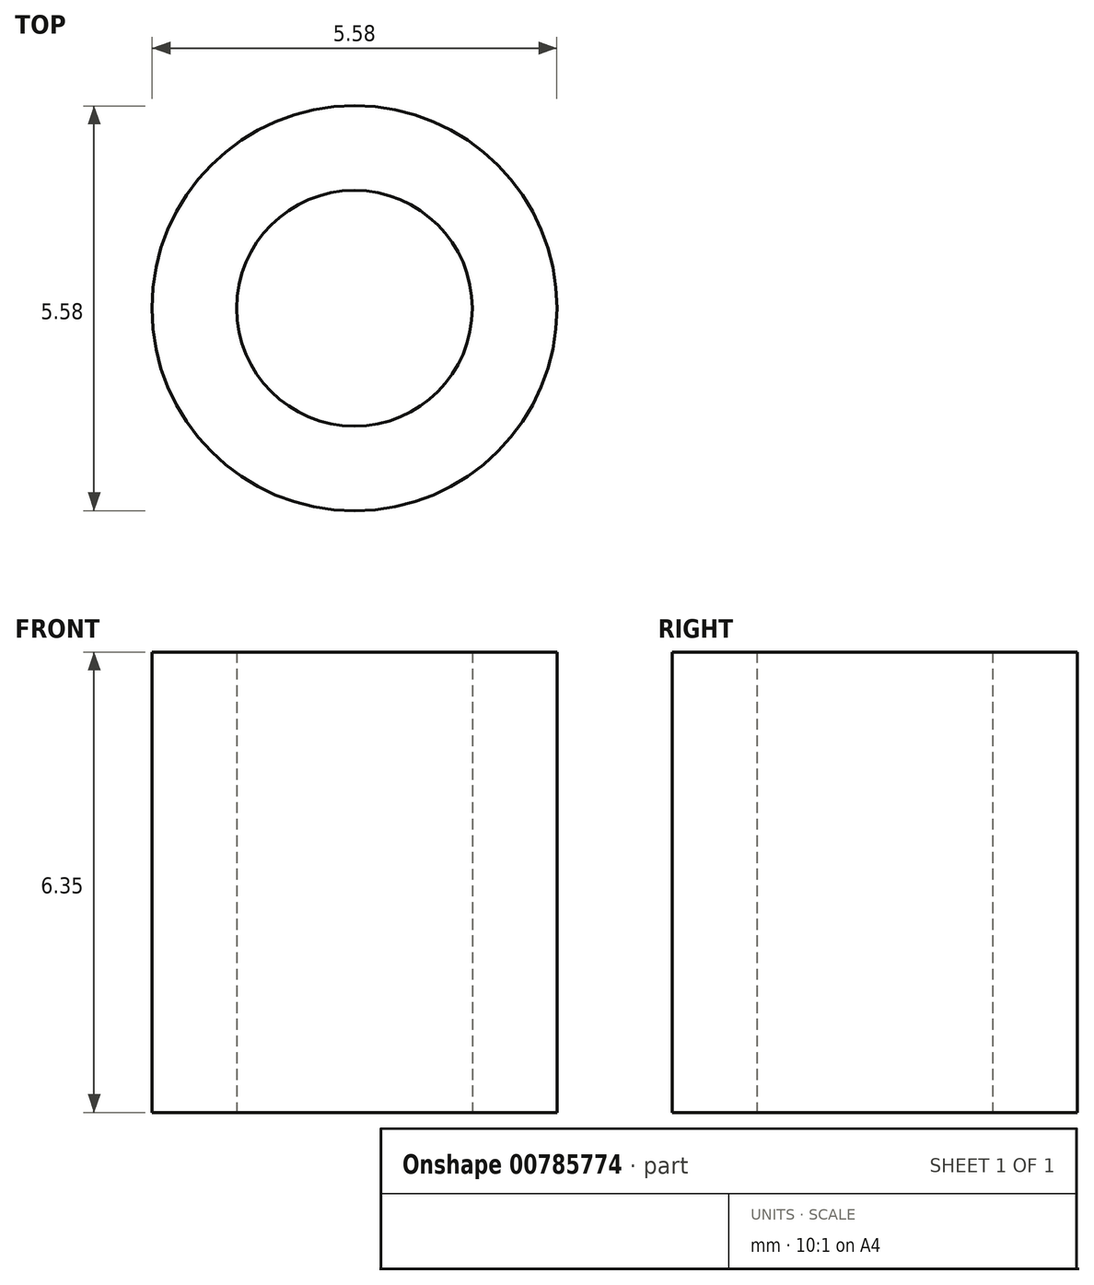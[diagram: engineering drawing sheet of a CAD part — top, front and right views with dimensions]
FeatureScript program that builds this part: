
annotation { "Feature Type Name" : "Feature", "Feature Type Description" : "" }
export const myFeature = defineFeature(function(context is Context, id is Id, definition is map)
    precondition{}
    {
        {
            var Q0;
            Q0=qCreatedBy(makeId("Top.planeOp"),FACE);
            var sketch = newSketch(context, id + "F0", { "sketchPlane" : qUnion([Q0])});
            skCircle(sketch, "E0", {"center": v(0, 0) * mm, "radius": 2.8 * mm});
            skCircle(sketch, "E1", {"center": v(0, 0) * mm, "radius": 1.63 * mm});
            skSolve(sketch);
        }
        {
            var Q0;
            Q0=qSketchRegion(id+"F0",true);
            extrude(context, id + "F1", {"entities" : qUnion([Q0]), "depth" : 6.35 * mm, "offsetDistance" : 25.4 * mm});
        }
    });
